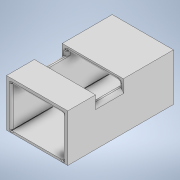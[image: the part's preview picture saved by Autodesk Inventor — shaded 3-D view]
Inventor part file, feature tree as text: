
AUTODESK INVENTOR PART (.ipt)
format: ipt  version: 2020 (Build 240168000, 168)  size: 323,584 bytes
history: native  units: in
note: dims shown in document units (in); Inventor stores cm internally (conversion verified against a paired STEP export)
features: extrude x9, sketch x9, projected_geometry x9, fillet x3
ambient origin geometry x8: Origin, YZ Plane, XZ Plane, XY Plane, X Axis, Y Axis, Z Axis, Center Point
bodies: Solid1 (feature_tree)
feature tree (30):
  extrude  "Extrusion1"  Depth=3.7402in
  extrude  "Extrusion2"  Depth=0.0984in
  extrude  "Extrusion3"  Depth=1.378in
  extrude  "Extrusion4"  Depth=1.7717in
  extrude  "Extrusion5"  Depth=0.2362in TaperAngle=0.0deg
  extrude  "Extrusion6"  Depth=0.2362in TaperAngle=0.0deg
  extrude  "Extrusion7"  Depth=0.0984in TaperAngle=0.0deg
  extrude  "Extrusion9"  Depth=0.0197in
  extrude  "Extrusion10"  Depth=0.1181in
  fillet  "Fillet1"  Radius=0.0197in
  fillet  "Fillet3"  [1 undecoded]
  fillet  "Fillet4"  Radius=0.0787in
  sketch  "Sketch1"  dims[d0=1.9685in d1=3.7402in]
  sketch  "Sketch2"  dims[d2=1.5748in d3=0.0in d4=0.0984in]
  projected_geometry  "Projected Loop1"
  sketch  "Sketch3"  dims[d5=1.7717in d6=1.378in]
  projected_geometry  "Projected Loop2"
  sketch  "Sketch4"  dims[d7=3.5433in d8=0.0in d9=1.7717in]
  projected_geometry  "Projected Loop3"
  sketch  "Sketch5"  dims[d10=2.7559in d11=0.2362in d12=0.0in]
  projected_geometry  "Projected Loop4"
  sketch  "Sketch6"  dims[d13=0.9843in d14=0.2362in d15=0.0in]
  projected_geometry  "Projected Loop5"
  sketch  "Sketch7"  dims[d16=0.0984in d17=0.0in d18=0.0984in d19=0.0in]
  projected_geometry  "Projected Loop6"
  projected_geometry  "Projected Loop7"
  sketch  "Sketch10"  dims[d20=0.0984in d21=0.0in d29=0.0197in]
  projected_geometry  "Projected Loop9"
  sketch  "Sketch11"  dims[d30=0.0984in d31=0.0in d32=0.0197in d35=0.0197in d36=180.0deg d37=0.0787in d38=0.0197in d43=0.0591in d44=0.0197in d45=0.0984in d46=0.0in d47=0.0197in d48=0.0197in d49=0.0787in d51=0.1181in d52=0.1181in]
  projected_geometry  "Projected Loop10"
note: 1 required parameter value undecoded (feature->parameter linkage not recoverable at this tier; creation-order binding heuristic only, values carry confidence <= 0.55)
